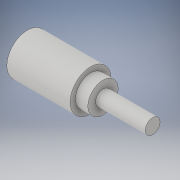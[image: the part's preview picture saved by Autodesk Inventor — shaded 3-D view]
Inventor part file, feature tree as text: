
AUTODESK INVENTOR PART (.ipt)
format: ipt  version: 2019 (Build 230136000, 136)  size: 116,224 bytes
history: native  units: mm
features: sketch x3, extrude x2, sheet_metal_op x1, other x1
ambient origin geometry x8: Origin, YZ Plane, XZ Plane, XY Plane, X Axis, Y Axis, Z Axis, Center Point
bodies: Solid1 (feature_tree)
feature tree (7):
  sheet_metal_op  "Face1"
  extrude  "Extrusion1"  Depth=25.5mm
  extrude  "Extrusion2"  Depth=5.0mm TaperAngle=0.0deg
  sketch  "Sketch1"  dims[d0=16.5mm d1=25.5mm]
  other  "Plate1"
  sketch  "Sketch2"  dims[d2=12.19mm d3=5.0mm d4=0.0mm]
  sketch  "Sketch3"  dims[d5=6.0mm d6=20.0mm d7=0.0mm]
